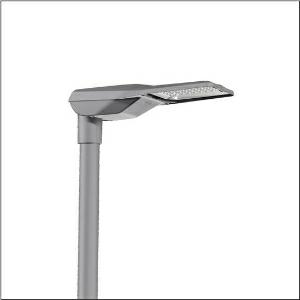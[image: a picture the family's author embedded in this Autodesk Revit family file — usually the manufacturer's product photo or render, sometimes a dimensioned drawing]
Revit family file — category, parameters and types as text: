
# Revit family: streetlight_sl_21_iq_mini___stw1_0a_5xe2e41g08hb_6f26
name_source: partatom
category: Lighting Fixtures
units: mm (PartAtom-declared; Revit-internal decimal feet)

## family parameters
Cut with Voids When Loaded = No
Host = Face
Light Source = No
Part Type = Normal
Room Calculation Point = No
Round Connector Dimension = Use Diameter
Shared = No

## types (1)
- --- (1 x LED, 9860 lm, 70.9 W, 4000K)
    Apparent Load = 71 VA
    CIE Flux Codes = 38 75 98 100 100
    Color Rendering = 70
    Color Temperature = 4000K
    Default Elevation = 1800 mm
    Description = Streetlight SL 21 iQ mini, mast luminaire, primary light control with lens, of PMMA, primary optical cover: cover, of toughened safety glass, transparent, light distribution: STW1.0a, light emission: direct distribution, primary light characteristic: asymmetric, installation type: post-top, side-entry, LED, High Power LED, rated luminous flux: 9.860lm, luminous efficacy: 139lm/W, light colour: 740, colour temperature: 4000K, control gear: iQ Street-Remote, control: Street-Remote, Auto-Match, Temp-Guard, Lumen-Switch, Night-Set, Smart-Wire, Light-Fading, Desk-Remote (wireless, voltage-free reading and setting of iQ features in the workshop via application-optimized NFC function/RFID function), optimised constant luminous flux control (CLO 2.0), pre-setting: linear dimming characteristic, mains connection: 220..240V, AC, 50/60Hz, start of lifetime: 71W, end of service life: 75W, reduction: 31W, luminaire housing, of diecast aluminium, powder-coated, Siteco® metallic grey (DB 702S), corrosivity category C5 mid according to DIN EN ISO 12944, please order mast flange separately, inclination adjustable: 0°, 5°, 10°, 15°, sealing non-destructively replaceable, multi-level sealing system, length: 628mm, width: 235mm, height: 110mm, mast flange for spigot size: 42mm (side-entry): 5XC10008XM4, 60/48mm (side-entry/post-top): 5XC10108XM2, 76/60mm (side-entry/post-top): 5XC10108XM1, mounting height: 4..8m, protection rating (complete): IP66, insulation class (complete): insulation class II (safety insulation), certification: CE, ENEC, ENEC+, VDE, impact resistance: IK10, permissible operating ambient temperature for outdoor applications: -40..+50°C, standard-compliant lighting for roads and squares, packaging unit: 1 piece

Light Distribution: STW1.0a
    Height = 110 mm
    Lamp = 1 x LED
    Lamp Light Flux = 9860 lm
    Lamp Power = 70.9 W
    Lamp count = 1
    Length = 625 mm
    Luminous efficacy = 139 lm/W
    Manufacturer = Siteco
    ModVariant = No
    Model = 5XE2E41G08HB
    Number of Poles = 1
    OnlyDefault = Yes
    Power Factor = 1
    Product Name = Streetlight SL 21 iQ mini | STW1.0a
    Product group = mast luminaire | pylon top
    ProductGroupID = 6100
    Protection Class = Protection class II
    Protection Degree = IP 66
    RLX_Detail_Level = 1
    RLX_Emergency_Light_Flux = 0 lm
    RLX_Emergency_Type = 0
    RLX_Emergency_Type_DB = No
    RlxData = <blob elided: 26365 chars, md5=cf30f9b4>
    Socket = socket
    Standby Power = 0 W
    System Light Flux = 9860 lm
    System Power = 71 W
    Type Comments = factory setting: luminous flux: 100 % | dim-lin: 254 | 711 mA
    Type Image = l_1003519.jpg
    URL = http://relux.com
    VarID = @adj_179211
    Voltage = 0 V
    Weight = 0.00 kg
    Width = 234 mm

## geometry (parser evidence)
native form markers: Blend x4, Sweep x12
no freeform markers — native parametric forms only
